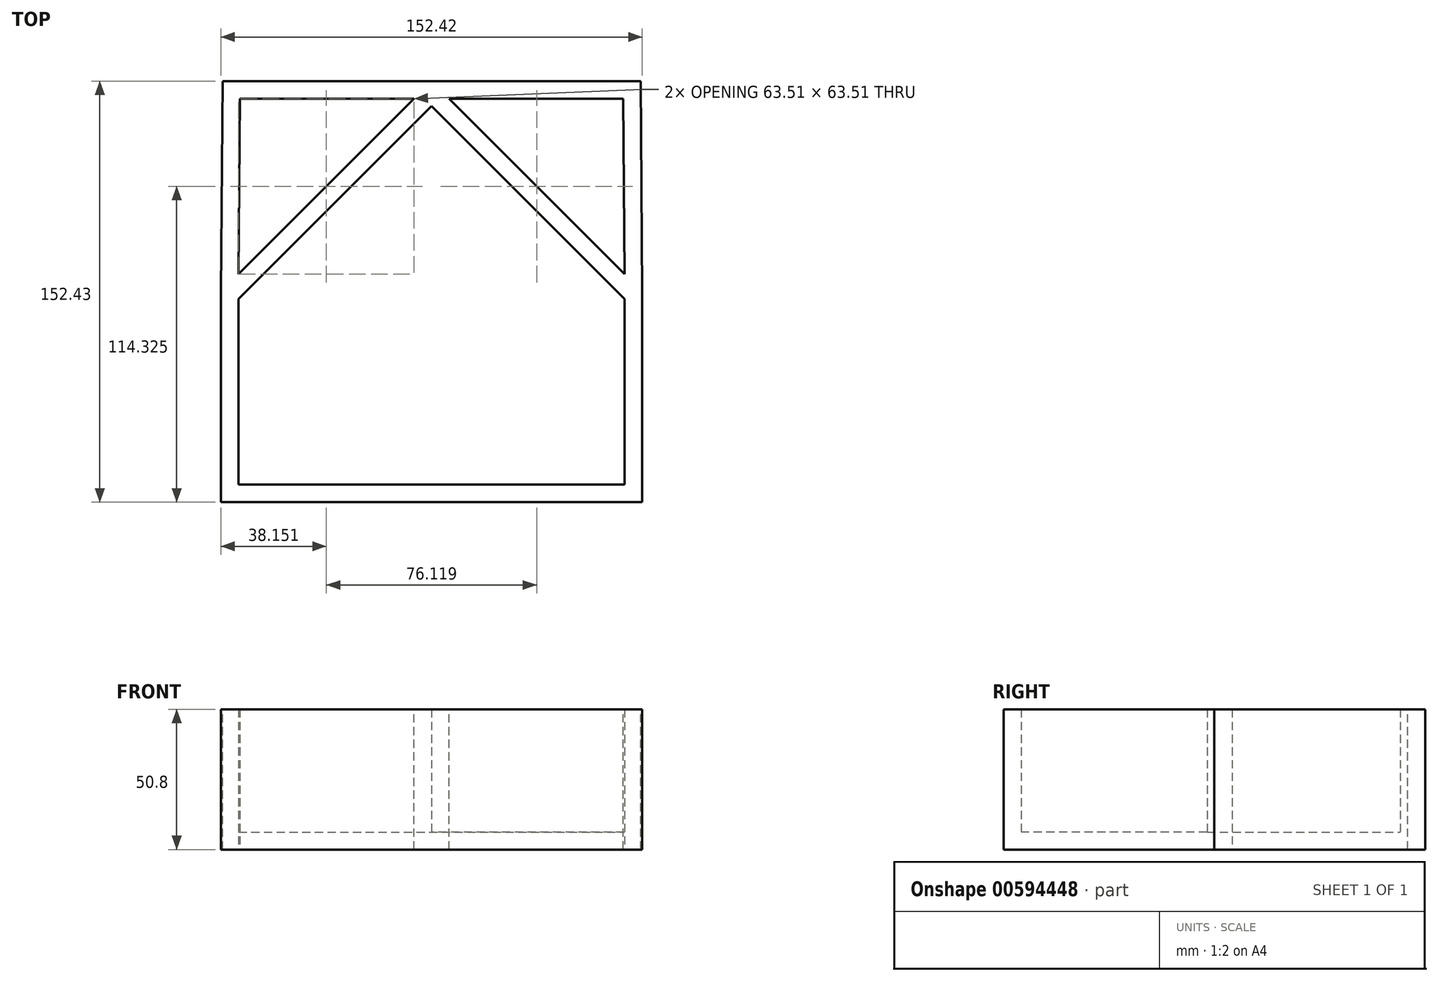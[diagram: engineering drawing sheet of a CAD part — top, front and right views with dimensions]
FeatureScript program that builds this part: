
annotation { "Feature Type Name" : "Feature", "Feature Type Description" : "" }
export const myFeature = defineFeature(function(context is Context, id is Id, definition is map)
    precondition{}
    {
        {
            var Q0;
            Q0=qCreatedBy(makeId("Top.planeOp"),FACE);
            var sketch = newSketch(context, id + "F0", { "sketchPlane" : qUnion([Q0])});
            skLineSegment(sketch, "E0.bottom", {"start": v(-76.2, 76.2) * mm, "end": v(76.2, 76.2) * mm});
            skLineSegment(sketch, "E0.top", {"start": v(-76.2, -76.2) * mm, "end": v(76.2, -76.2) * mm});
            skLineSegment(sketch, "E0.left", {"start": v(-76.2, 76.2) * mm, "end": v(-76.2, -76.2) * mm});
            skLineSegment(sketch, "E0.right", {"start": v(76.2, 76.2) * mm, "end": v(76.2, -76.2) * mm});
            skPoint(sketch, "E0.middle", {"position": v(0, 0) * mm});
            skLineSegment(sketch, "E1", {"start": v(-76.2, 0) * mm, "end": v(0, 76.2) * mm});
            skLineSegment(sketch, "E2", {"start": v(76.2, 0) * mm, "end": v(0, 76.2) * mm});
            skSolve(sketch);
        }
        {
            var Q0;
            {var subQ1=sQuery(id+"F0.wireOp",EDGE,"E0.top");Q0=makeQuery(id+"F0.imprint","IMPRINT",FACE,{"disambiguationData":[TD([[makeQuery(id+"F0.imprint","IMPRINT",EDGE,{"derivedFrom":subQ1}),1.0]])]});}
            extrude(context, id + "F1", {"entities" : qUnion([Q0]), "depth" : 50.8 * mm, "offsetDistance" : 25.4 * mm});
        }
        {
            var Q0;
            Q0=makeQuery(id+"F1.opExtrude","CAP_FACE",FACE,{"disambiguationData":[OSD([sQuery(id+"F0.wireOp",EDGE,"E0.top"),sQuery(id+"F0.wireOp",EDGE,"E0.left"),sQuery(id+"F0.wireOp",EDGE,"E0.right"),sQuery(id+"F0.wireOp",EDGE,"E1"),sQuery(id+"F0.wireOp",EDGE,"E2")])],"isStart":false});
            shell(context, id + "F2", {"entities" : qUnion([Q0]), "thickness" : 6.35 * mm});
        }
        {
            var Q0;
            Q0=qCreatedBy(makeId("Top.planeOp"),FACE);
            var sketch = newSketch(context, id + "F3", { "sketchPlane" : qUnion([Q0])});
            skLineSegment(sketch, "E3", {"start": v(0, 76.24) * mm, "end": v(75.63, 76.24) * mm});
            skLineSegment(sketch, "E4", {"start": v(75.63, 76.24) * mm, "end": v(76.21, 0) * mm});
            skSolve(sketch);
        }
        {
            var Q0;
            Q0 = qSketchRegion(id + "F3", true);
            var Q1;
            Q1=sQuery(id+"F3.wireOp",EDGE,"E4");
            var Q2;
            Q2=sQuery(id+"F3.wireOp",EDGE,"E3");
            extrude(context, id + "F4", {"entities" : qUnion([Q0]), "bodyType" : ToolBodyType.SURFACE, "surfaceEntities" : qUnion([Q1, Q2]), "depth" : 50.8 * mm, "offsetDistance" : 25.4 * mm});
        }
        {
            var Q0;
            Q0=makeQuery(id+"F4.opExtrude","SWEPT_FACE",FACE,{"disambiguationData":[OSD([sQuery(id+"F3.wireOp",EDGE,"E4")])]});
            extrude(context, id + "F5", {"entities" : qUnion([Q0]), "operationType" : NewBodyOperationType.ADD, "depth" : 6.35 * mm, "offsetDistance" : 25.4 * mm});
        }
        {
            var Q0;
            Q0=makeQuery(id+"F4.opExtrude","SWEPT_FACE",FACE,{"disambiguationData":[OSD([sQuery(id+"F3.wireOp",EDGE,"E3")])]});
            extrude(context, id + "F6", {"entities" : qUnion([Q0]), "operationType" : NewBodyOperationType.ADD, "depth" : 6.35 * mm, "offsetDistance" : 25.4 * mm});
        }
        {
            var Q0;
            Q0=makeQuery(id+"F4.opExtrude","SWEPT_BODY",BODY,{"disambiguationData":[OSD([sQuery(id+"F3.wireOp",EDGE,"E3")])]});
            var Q1;
            Q1=qCreatedBy(makeId("Right.planeOp"),FACE);
            mirror(context, id + "F7", {"entities" : qUnion([Q0]), "mirrorPlane" : qUnion([Q1])});
        }
        {
            var Q0;
            Q0=makeQuery(id+"F7.opPattern","COPY",FACE,{"derivedFrom":makeQuery(id+"F4.opExtrude","SWEPT_FACE",FACE,{"disambiguationData":[OSD([sQuery(id+"F3.wireOp",EDGE,"E4")])]}),"instanceName":"1"});
            extrude(context, id + "F8", {"entities" : qUnion([Q0]), "operationType" : NewBodyOperationType.ADD, "depth" : 6.35 * mm, "offsetDistance" : 25.4 * mm});
        }
        {
            var Q0;
            Q0=makeQuery(id+"F7.opPattern","COPY",FACE,{"derivedFrom":makeQuery(id+"F4.opExtrude","SWEPT_FACE",FACE,{"disambiguationData":[OSD([sQuery(id+"F3.wireOp",EDGE,"E3")])]}),"instanceName":"1"});
            extrude(context, id + "F9", {"entities" : qUnion([Q0]), "operationType" : NewBodyOperationType.ADD, "depth" : 6.35 * mm, "offsetDistance" : 25.4 * mm});
        }
    });
